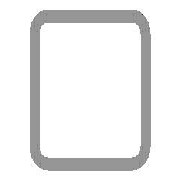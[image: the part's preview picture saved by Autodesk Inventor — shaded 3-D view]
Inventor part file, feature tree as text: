
AUTODESK INVENTOR PART (.ipt)
format: ipt  version: 2025 (Build 290162010, 162A)  size: 130,048 bytes
history: native  units: mm (DEFAULTED — no unit token found)
features: other x3, sketch x1, plane x1
ambient origin geometry x8: Origin, YZ Plane, XZ Plane, XY Plane, X Axis, Y Axis, Z Axis, Center Point
bodies: Solid1 (feature_tree), Body (feature_tree)
feature tree (5):
  other  "Driven Length"
  other  "Start plane"
  other  "End plane"
  sketch  "Sketch3"  dims[d3=2925.0mm d4=0.0mm d7=6.0mm d9=80.0mm d11=80.0mm d12=3.0mm d13=-0.0mm d14=2925.0mm d15=40.0mm d16=40.0mm d17=90.0deg d18=2925.0mm]
  plane  "Work Plane3"
